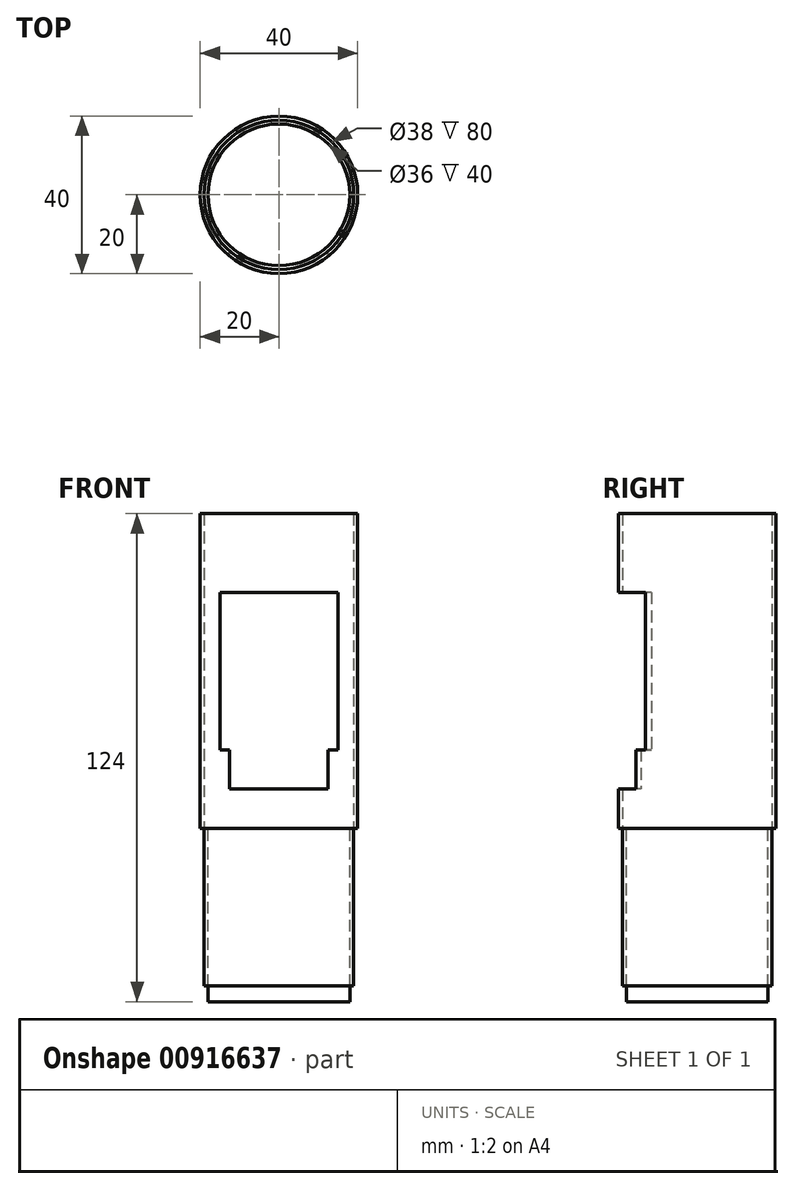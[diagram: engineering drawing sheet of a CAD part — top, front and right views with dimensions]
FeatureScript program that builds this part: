
annotation { "Feature Type Name" : "Feature", "Feature Type Description" : "" }
export const myFeature = defineFeature(function(context is Context, id is Id, definition is map)
    precondition{}
    {
        {
            var Q0;
            Q0=qCreatedBy(makeId("Top.planeOp"),FACE);
            var sketch = newSketch(context, id + "F0", { "sketchPlane" : qUnion([Q0])});
            skCircle(sketch, "E0", {"center": v(0, 0) * mm, "radius": 19 * mm});
            skCircle(sketch, "E1", {"center": v(0, 0) * mm, "radius": 20 * mm});
            skSolve(sketch);
        }
        {
            var Q0;
            Q0=makeQuery(id+"F0.imprint","IMPRINT",FACE,{"disambiguationData":[TD([[makeQuery(id+"F0.imprint","IMPRINT",EDGE,{"derivedFrom":sQuery(id+"F0.wireOp",EDGE,"E0")}),-1.0]])]});
            extrude(context, id + "F1", {"entities" : qUnion([Q0]), "depth" : 80 * mm, "offsetDistance" : 25 * mm});
        }
        {
            var Q0;
            Q0=qCreatedBy(makeId("Front.planeOp"),FACE);
            cPlane(context, id + "F2", {"entities" : qUnion([Q0]), "cplaneType" : CPlaneType.OFFSET, "offset" : 20 * mm, "width" : 150 * mm, "height" : 150 * mm});
        }
        {
            var Q0;
            Q0=qCreatedBy(id+"F2.planeOp",FACE);
            var sketch = newSketch(context, id + "F3", { "sketchPlane" : qUnion([Q0])});
            skLineSegment(sketch, "E2.bottom", {"start": v(-15, 60) * mm, "end": v(15, 60) * mm});
            skLineSegment(sketch, "E2.top", {"start": v(-15, 20) * mm, "end": v(15, 20) * mm});
            skLineSegment(sketch, "E2.left", {"start": v(-15, 60) * mm, "end": v(-15, 20) * mm});
            skLineSegment(sketch, "E2.right", {"start": v(15, 60) * mm, "end": v(15, 20) * mm});
            skSolve(sketch);
        }
        {
            var Q0;
            Q0=makeQuery(id+"F3.imprint","IMPRINT",FACE,{"disambiguationData":[TD([[makeQuery(id+"F3.imprint","IMPRINT",EDGE,{"derivedFrom":sQuery(id+"F3.wireOp",EDGE,"E2.bottom")}),-1.0]])]});
            extrude(context, id + "F4", {"entities" : qUnion([Q0]), "operationType" : NewBodyOperationType.REMOVE, "oppositeDirection" : true, "depth" : 25 * mm, "offsetDistance" : 25 * mm});
        }
        {
            var Q0;
            Q0=makeQuery(id+"F1.opExtrude","CAP_FACE",FACE,{"disambiguationData":[OSD([sQuery(id+"F0.wireOp",EDGE,"E0"),sQuery(id+"F0.wireOp",EDGE,"E1")])],"isStart":true});
            var sketch = newSketch(context, id + "F5", { "sketchPlane" : qUnion([Q0])});
            skArc(sketch, "E3", {"start": v(19, 0) * mm, "mid": v(0, 19) * mm, "end": v(-19, 0) * mm});
            skArc(sketch, "E4", {"start": v(18, 0) * mm, "mid": v(0, 18) * mm, "end": v(-18, 0) * mm});
            skLineSegment(sketch, "E5", {"start": v(-19, 0) * mm, "end": v(-18, 0) * mm});
            skLineSegment(sketch, "E6", {"start": v(18, 0) * mm, "end": v(19, 0) * mm});
            skSolve(sketch);
        }
        {
            var Q0;
            Q0=makeQuery(id+"F5.imprint","IMPRINT",FACE,{"disambiguationData":[TD([[makeQuery(id+"F5.imprint","IMPRINT",EDGE,{"derivedFrom":sQuery(id+"F5.wireOp",EDGE,"E3")}),-1.0]])]});
            extrude(context, id + "F6", {"entities" : qUnion([Q0]), "oppositeDirection" : true, "depth" : 60 * mm, "offsetDistance" : 25 * mm});
        }
        {
            var Q0;
            Q0=qCreatedBy(id+"F2.planeOp",FACE);
            var sketch = newSketch(context, id + "F7", { "sketchPlane" : qUnion([Q0])});
            skLineSegment(sketch, "E7.bottom", {"start": v(-12.5, 45) * mm, "end": v(12.5, 45) * mm});
            skLineSegment(sketch, "E7.top", {"start": v(-12.5, 10) * mm, "end": v(12.5, 10) * mm});
            skLineSegment(sketch, "E7.left", {"start": v(-12.5, 45) * mm, "end": v(-12.5, 10) * mm});
            skLineSegment(sketch, "E7.right", {"start": v(12.5, 45) * mm, "end": v(12.5, 10) * mm});
            skSolve(sketch);
        }
        {
            var Q0;
            Q0=makeQuery(id+"F7.imprint","IMPRINT",FACE,{"disambiguationData":[TD([[makeQuery(id+"F7.imprint","IMPRINT",EDGE,{"derivedFrom":sQuery(id+"F7.wireOp",EDGE,"E7.bottom")}),-1.0]])]});
            extrude(context, id + "F8", {"entities" : qUnion([Q0]), "operationType" : NewBodyOperationType.REMOVE, "oppositeDirection" : true, "depth" : 10 * mm, "offsetDistance" : 25 * mm});
        }
        {
            var Q0;
            Q0=makeQuery(id+"F6.opExtrude","SWEPT_BODY",BODY,{"disambiguationData":[OSD([sQuery(id+"F5.wireOp",EDGE,"E3"),sQuery(id+"F5.wireOp",EDGE,"E4"),sQuery(id+"F5.wireOp",EDGE,"E5"),sQuery(id+"F5.wireOp",EDGE,"E6")])]});
            deleteBodies(context, id + "F9", {"entities" : qUnion([Q0])});
        }
        {
            var Q0;
            Q0=makeQuery(id+"F1.opExtrude","CAP_FACE",FACE,{"disambiguationData":[OSD([sQuery(id+"F0.wireOp",EDGE,"E0"),sQuery(id+"F0.wireOp",EDGE,"E1")])],"isStart":true});
            var sketch = newSketch(context, id + "F10", { "sketchPlane" : qUnion([Q0])});
            skCircle(sketch, "E8", {"center": v(0, 0) * mm, "radius": 19 * mm});
            skCircle(sketch, "E9", {"center": v(0, 0) * mm, "radius": 18 * mm});
            skSolve(sketch);
        }
        {
            var Q0;
            Q0=makeQuery(id+"F10.imprint","IMPRINT",FACE,{"disambiguationData":[TD([[makeQuery(id+"F10.imprint","IMPRINT",EDGE,{"derivedFrom":sQuery(id+"F10.wireOp",EDGE,"E8")}),-1.0]])]});
            extrude(context, id + "F11", {"entities" : qUnion([Q0]), "depth" : 40 * mm, "offsetDistance" : 25 * mm});
        }
        {
            var Q0;
            Q0=makeQuery(id+"F11.opExtrude","CAP_FACE",FACE,{"disambiguationData":[OSD([sQuery(id+"F10.wireOp",EDGE,"E8"),sQuery(id+"F10.wireOp",EDGE,"E9")])],"isStart":false});
            var sketch = newSketch(context, id + "F12", { "sketchPlane" : qUnion([Q0])});
            skCircle(sketch, "E10", {"center": v(0, 0) * mm, "radius": 18 * mm});
            skSolve(sketch);
        }
        {
            var Q0;
            Q0=makeQuery(id+"F12.imprint","IMPRINT",FACE,{"disambiguationData":[TD([[makeQuery(id+"F12.imprint","IMPRINT",EDGE,{"derivedFrom":sQuery(id+"F12.wireOp",EDGE,"E10")}),1.0]])]});
            extrude(context, id + "F13", {"entities" : qUnion([Q0]), "depth" : 4 * mm, "offsetDistance" : 25 * mm});
        }
    });
